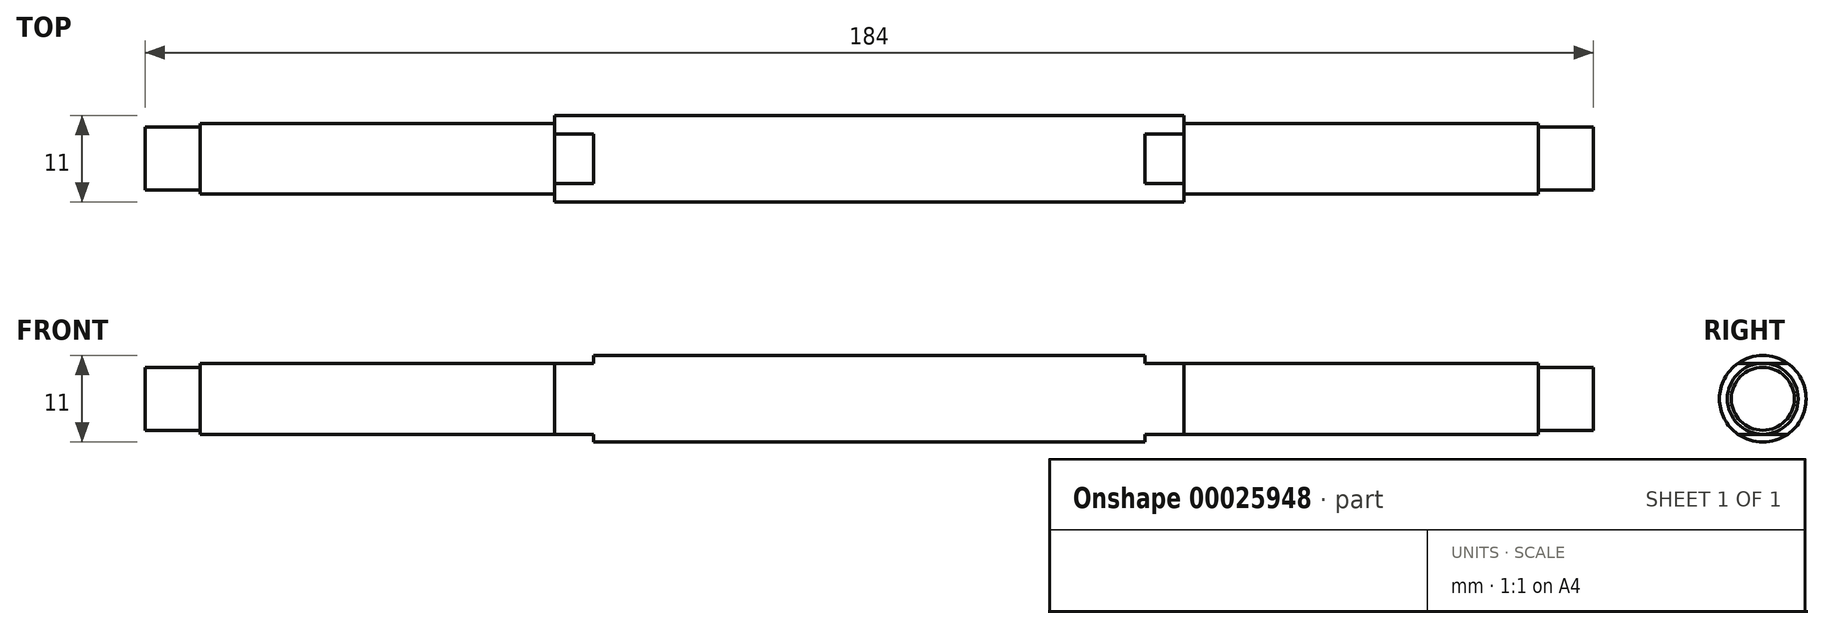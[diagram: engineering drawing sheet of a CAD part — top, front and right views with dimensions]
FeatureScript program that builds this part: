
annotation { "Feature Type Name" : "Feature", "Feature Type Description" : "" }
export const myFeature = defineFeature(function(context is Context, id is Id, definition is map)
    precondition{}
    {
        {
            var Q0;
            Q0=qCreatedBy(makeId("Right.planeOp"),FACE);
            var sketch = newSketch(context, id + "F0", { "sketchPlane" : qUnion([Q0])});
            skCircle(sketch, "E0", {"center": v(0, 0) * mm, "radius": 4 * mm});
            skSolve(sketch);
        }
        {
            var Q0;
            Q0=makeQuery(id+"F0.imprint","IMPRINT",FACE,{"disambiguationData":[TD([[makeQuery(id+"F0.imprint","IMPRINT",EDGE,{"derivedFrom":sQuery(id+"F0.wireOp",EDGE,"E0")}),1.0]])]});
            extrude(context, id + "F1", {"entities" : qUnion([Q0]), "depth" : 7 * mm});
        }
        {
            var Q0;
            Q0=makeQuery(id+"F1.opExtrude","CAP_FACE",FACE,{"disambiguationData":[OSD([sQuery(id+"F0.wireOp",EDGE,"E0")])],"isStart":false});
            var sketch = newSketch(context, id + "F2", { "sketchPlane" : qUnion([Q0])});
            skCircle(sketch, "E1", {"center": v(0, 0) * mm, "radius": 4.5 * mm});
            skSolve(sketch);
        }
        {
            var Q0;
            Q0 = qSketchRegion(id + "F2", true);
            extrude(context, id + "F3", {"entities" : qUnion([Q0]), "operationType" : NewBodyOperationType.ADD, "depth" : 45 * mm});
        }
        {
            var Q0;
            Q0=makeQuery(id+"F3.opExtrude","CAP_FACE",FACE,{"disambiguationData":[OSD([sQuery(id+"F2.wireOp",EDGE,"E1")])],"isStart":false});
            var sketch = newSketch(context, id + "F4", { "sketchPlane" : qUnion([Q0])});
            skCircle(sketch, "E2", {"center": v(0, 0) * mm, "radius": 4.5 * mm, "construction": true});
            skArc(sketch, "E3", {"start": v(-3.16, 4.5) * mm, "mid": v(-5.5, 0) * mm, "end": v(-3.16, -4.5) * mm});
            skLineSegment(sketch, "E4", {"start": v(-3.16, -4.5) * mm, "end": v(3.16, -4.5) * mm});
            skLineSegment(sketch, "E5.MirrorCS", {"start": v(-3.16, 4.5) * mm, "end": v(3.16, 4.5) * mm});
            skPoint(sketch, "E6.orphan", {"position": v(-7.07, 4.5) * mm});
            skPoint(sketch, "E7.orphan", {"position": v(-7.07, -4.5) * mm});
            skPoint(sketch, "E8.orphan", {"position": v(7.43, -4.5) * mm});
            skPoint(sketch, "E9.orphan", {"position": v(7.43, 4.5) * mm});
            skArc(sketch, "E10.trimOffspring", {"start": v(3.16, -4.5) * mm, "mid": v(5.5, 0) * mm, "end": v(3.16, 4.5) * mm});
            skSolve(sketch);
        }
        {
            var Q0;
            Q0 = qSketchRegion(id + "F4", true);
            extrude(context, id + "F5", {"entities" : qUnion([Q0]), "operationType" : NewBodyOperationType.ADD, "depth" : 5 * mm});
        }
        {
            var Q0;
            Q0=makeQuery(id+"F5.opExtrude","CAP_FACE",FACE,{"disambiguationData":[OSD([sQuery(id+"F4.wireOp",EDGE,"E3"),sQuery(id+"F4.wireOp",EDGE,"E4"),sQuery(id+"F4.wireOp",EDGE,"E5.MirrorCS"),sQuery(id+"F4.wireOp",EDGE,"E10.trimOffspring")])],"isStart":false});
            var sketch = newSketch(context, id + "F6", { "sketchPlane" : qUnion([Q0])});
            skCircle(sketch, "E11", {"center": v(0, 0) * mm, "radius": 5.5 * mm});
            skSolve(sketch);
        }
        {
            var Q0;
            Q0 = qSketchRegion(id + "F6", true);
            extrude(context, id + "F7", {"entities" : qUnion([Q0]), "operationType" : NewBodyOperationType.ADD, "depth" : 70 * mm});
        }
        {
            var Q0;
            Q0=makeQuery(id+"F7.opExtrude","CAP_FACE",FACE,{"disambiguationData":[OSD([sQuery(id+"F6.wireOp",EDGE,"E11")])],"isStart":false});
            var sketch = newSketch(context, id + "F8", { "sketchPlane" : qUnion([Q0])});
            skCircle(sketch, "E12", {"center": v(0, 0) * mm, "radius": 4.5 * mm, "construction": true});
            skArc(sketch, "E13", {"start": v(-3.16, 4.5) * mm, "mid": v(-5.5, 0) * mm, "end": v(-3.16, -4.5) * mm});
            skLineSegment(sketch, "E14", {"start": v(-3.16, -4.5) * mm, "end": v(3.16, -4.5) * mm});
            skLineSegment(sketch, "E15.MirrorCS", {"start": v(-3.16, 4.5) * mm, "end": v(3.16, 4.5) * mm});
            skPoint(sketch, "E16.orphan", {"position": v(-7.07, 4.5) * mm});
            skPoint(sketch, "E17.orphan", {"position": v(-7.07, -4.5) * mm});
            skPoint(sketch, "E18.orphan", {"position": v(7.43, -4.5) * mm});
            skPoint(sketch, "E19.orphan", {"position": v(7.43, 4.5) * mm});
            skArc(sketch, "E20.trimOffspring", {"start": v(3.16, -4.5) * mm, "mid": v(5.5, 0) * mm, "end": v(3.16, 4.5) * mm});
            skSolve(sketch);
        }
        {
            var Q0;
            Q0 = qSketchRegion(id + "F8", true);
            extrude(context, id + "F9", {"entities" : qUnion([Q0]), "operationType" : NewBodyOperationType.ADD, "depth" : 5 * mm});
        }
        {
            var Q0;
            Q0=makeQuery(id+"F9.opExtrude","CAP_FACE",FACE,{"disambiguationData":[OSD([sQuery(id+"F8.wireOp",EDGE,"E13"),sQuery(id+"F8.wireOp",EDGE,"E14"),sQuery(id+"F8.wireOp",EDGE,"E15.MirrorCS"),sQuery(id+"F8.wireOp",EDGE,"E20.trimOffspring")])],"isStart":false});
            var sketch = newSketch(context, id + "F10", { "sketchPlane" : qUnion([Q0])});
            skCircle(sketch, "E21", {"center": v(0, 0) * mm, "radius": 4.5 * mm});
            skSolve(sketch);
        }
        {
            var Q0;
            {var subQ0=sQuery(id+"F10.wireOp",EDGE,"E21");var subQ2=makeQuery(id+"F10.imprint","INTERSECT",VERTEX,{"derivedFrom":[makeQuery(id+"F9.opExtrude","CAP_EDGE",EDGE,{"disambiguationData":[OSD([sQuery(id+"F8.wireOp",EDGE,"E14")])],"isStart":false}),subQ0]});Q0=makeQuery(id+"F10.imprint","IMPRINT",FACE,{"disambiguationData":[TD([[makeQuery(id+"F10.imprint","IMPRINT",EDGE,{"disambiguationData":[TD([[subQ2,1.0]])],"derivedFrom":subQ0}),1.0]])]});}
            extrude(context, id + "F11", {"entities" : qUnion([Q0]), "operationType" : NewBodyOperationType.ADD, "depth" : 45 * mm});
        }
        {
            var Q0;
            Q0=makeQuery(id+"F11.opExtrude","CAP_FACE",FACE,{"disambiguationData":[OSD([sQuery(id+"F10.wireOp",EDGE,"E21")])],"isStart":false});
            var sketch = newSketch(context, id + "F12", { "sketchPlane" : qUnion([Q0])});
            skCircle(sketch, "E22", {"center": v(0, 0) * mm, "radius": 4 * mm});
            skSolve(sketch);
        }
        {
            var Q0;
            Q0 = qSketchRegion(id + "F12", true);
            extrude(context, id + "F13", {"entities" : qUnion([Q0]), "operationType" : NewBodyOperationType.ADD, "depth" : 7 * mm});
        }
    });
